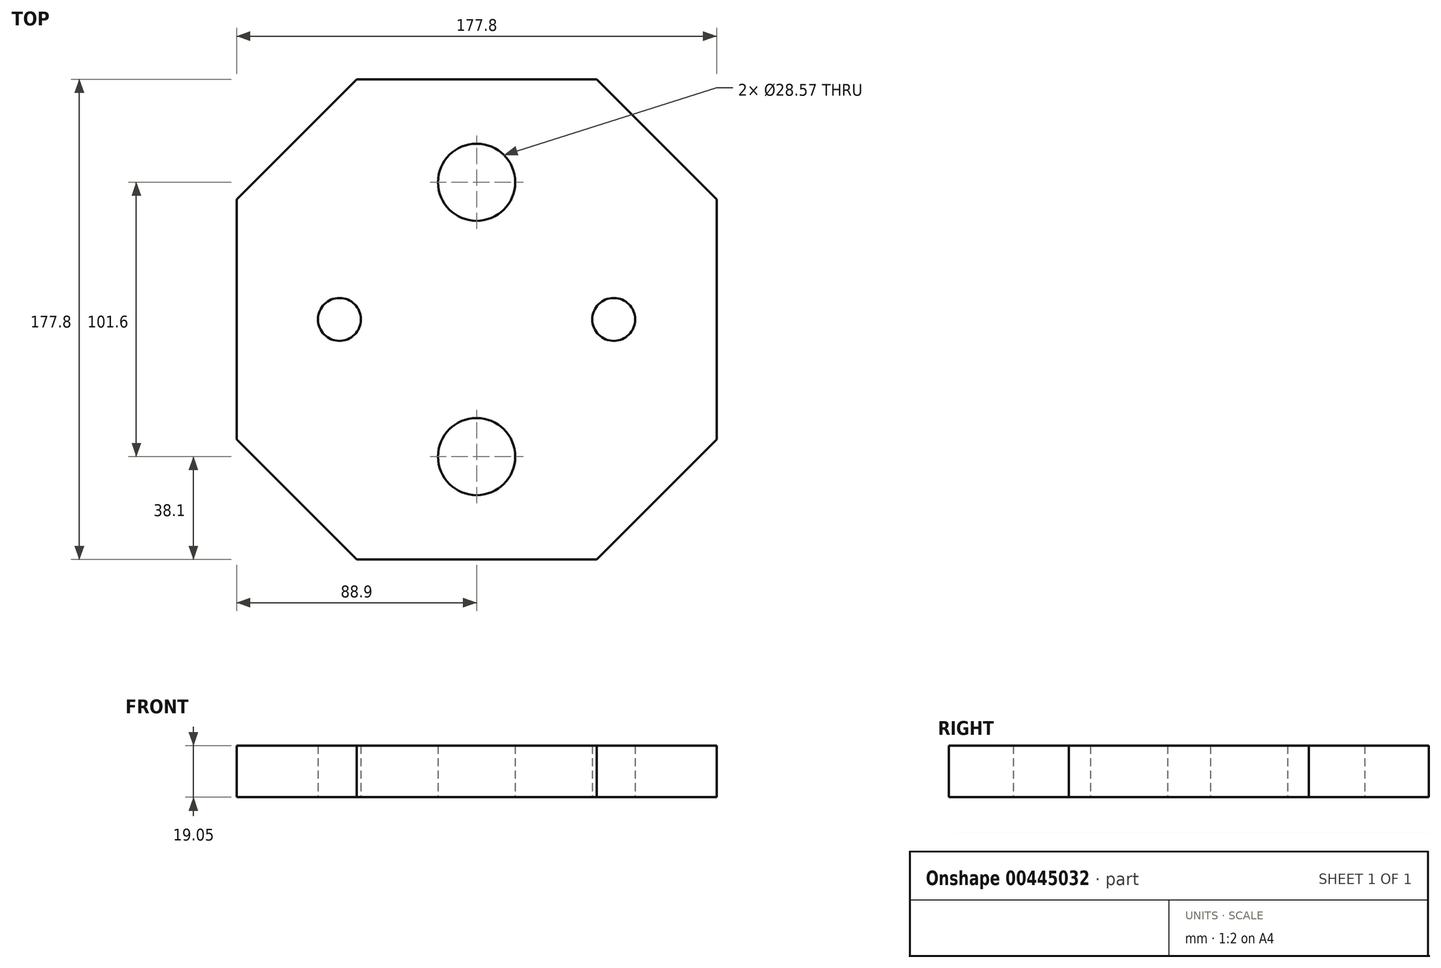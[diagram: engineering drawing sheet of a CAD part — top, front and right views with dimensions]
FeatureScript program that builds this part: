
annotation { "Feature Type Name" : "Feature", "Feature Type Description" : "" }
export const myFeature = defineFeature(function(context is Context, id is Id, definition is map)
    precondition{}
    {
        {
            var Q0;
            Q0=qCreatedBy(makeId("Top.planeOp"),FACE);
            var sketch = newSketch(context, id + "F0", { "sketchPlane" : qUnion([Q0])});
            skLineSegment(sketch, "E0.bottom", {"start": v(44.45, 88.9) * mm, "end": v(-44.45, 88.9) * mm});
            skLineSegment(sketch, "E0.top", {"start": v(44.45, -88.9) * mm, "end": v(-44.45, -88.9) * mm});
            skLineSegment(sketch, "E0.left", {"start": v(88.9, 44.45) * mm, "end": v(88.9, -44.45) * mm});
            skLineSegment(sketch, "E0.right", {"start": v(-88.9, 44.45) * mm, "end": v(-88.9, -44.45) * mm});
            skPoint(sketch, "E0.middle", {"position": v(0, 0) * mm});
            skLineSegment(sketch, "E1", {"start": v(-44.45, 88.9) * mm, "end": v(-88.9, 44.45) * mm});
            skLineSegment(sketch, "E2.MirrorCS", {"start": v(44.45, 88.9) * mm, "end": v(88.9, 44.45) * mm});
            skLineSegment(sketch, "E3.MirrorCS", {"start": v(-44.45, -88.9) * mm, "end": v(-88.9, -44.45) * mm});
            skLineSegment(sketch, "E4.MirrorCS", {"start": v(44.45, -88.9) * mm, "end": v(88.9, -44.45) * mm});
            skPoint(sketch, "E5.orphan", {"position": v(-88.9, 88.9) * mm});
            skPoint(sketch, "E6.orphan", {"position": v(-88.9, -88.9) * mm});
            skPoint(sketch, "E7.orphan", {"position": v(88.9, -88.9) * mm});
            skPoint(sketch, "E8.orphan", {"position": v(88.9, 88.9) * mm});
            skCircle(sketch, "E9", {"center": v(0, 50.8) * mm, "radius": 14.29 * mm});
            skCircle(sketch, "E10.MirrorC", {"center": v(0, -50.8) * mm, "radius": 14.29 * mm});
            skCircle(sketch, "E11", {"center": v(50.8, 0) * mm, "radius": 7.94 * mm});
            skCircle(sketch, "E12.MirrorC", {"center": v(-50.8, 0) * mm, "radius": 7.94 * mm});
            skSolve(sketch);
        }
        {
            var Q0;
            Q0=makeQuery(id+"F0.imprint","IMPRINT",FACE,{"disambiguationData":[TD([[makeQuery(id+"F0.imprint","IMPRINT",EDGE,{"derivedFrom":sQuery(id+"F0.wireOp",EDGE,"E0.bottom")}),1.0]])]});
            extrude(context, id + "F1", {"entities" : qUnion([Q0]), "depth" : 19.05 * mm});
        }
    });
